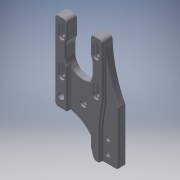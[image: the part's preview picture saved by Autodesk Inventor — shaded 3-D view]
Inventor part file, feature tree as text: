
AUTODESK INVENTOR PART (.ipt)
format: ipt  version: 2018 (Build 220112000, 112)  size: 500,224 bytes
history: native  units: in
note: dims shown in document units (in); Inventor stores cm internally (conversion verified against a paired STEP export)
features: extrude x12, sketch x12, projected_geometry x4, fillet x3, plane x2
ambient origin geometry x8: Origin, YZ Plane, XZ Plane, XY Plane, X Axis, Y Axis, Z Axis, Center Point
bodies: Solid1 (feature_tree)
feature tree (33):
  extrude  "Extrusion1"  Depth=1.6929in
  extrude  "Extrusion2"  Depth=0.4331in
  fillet  "Fillet1"  Radius=1.6535in
  extrude  "Extrusion3"  Depth=1.2205in
  extrude  "Extrusion4"  Depth=0.126in
  extrude  "Extrusion5"  Depth=0.315in
  extrude  "Extrusion6"  Depth=0.2362in TaperAngle=0.0deg
  plane  "Work Plane1"
  plane  "Work Plane2"
  extrude  "Extrusion7"  Depth=0.1575in TaperAngle=0.0deg
  extrude  "Extrusion8"  Depth=0.2362in
  extrude  "Extrusion9"  Depth=0.9449in
  extrude  "Extrusion10"  Depth=0.6102in
  extrude  "Extrusion11"  Depth=1.2992in
  extrude  "Extrusion12"  Depth=0.0394in
  fillet  "Fillet2"  Radius=7.0866in
  fillet  "Fillet4"  Radius=0.2362in
  sketch  "Sketch1"  dims[d0=3.8189in d1=1.6929in]
  sketch  "Sketch2"  dims[d2=0.4331in d3=0.4331in d4=1.6535in]
  sketch  "Sketch3"  dims[d5=0.1969in d6=0.0in d7=1.2205in]
  projected_geometry  "Projected Loop1"
  sketch  "Sketch4"  dims[d8=1.2205in d9=0.126in]
  projected_geometry  "Projected Loop2"
  sketch  "Sketch5"  dims[d10=0.2756in d11=0.315in]
  projected_geometry  "Projected Loop3"
  sketch  "Sketch6"  dims[d12=0.315in d13=0.2362in d14=0.0in]
  sketch  "Sketch8"  dims[d15=0.315in d16=0.1575in d17=0.0in]
  sketch  "Sketch9"  dims[d18=0.2362in d20=0.2362in]
  sketch  "Sketch10"  dims[d21=0.0787in d22=0.0in d23=0.9449in]
  projected_geometry  "Projected Loop4"
  sketch  "Sketch11"  dims[d24=0.315in d25=0.6102in]
  sketch  "Sketch12"  dims[d26=0.0in d27=0.0in d28=1.2992in]
  sketch  "Sketch13"  dims[d30=0.2362in d31=0.0in d32=0.1181in d33=7.0866in d34=0.2362in d35=0.0in d36=0.1654in d38=0.3937in d39=0.315in d40=0.4724in d41=0.2362in d42=0.0in d43=0.2165in d44=0.1654in d46=0.2165in d47=0.3937in d50=0.2362in d51=0.0in d52=0.2441in d53=0.0787in d54=0.0in d55=0.0787in d56=0.0in d57=0.7874in d58=0.3937in d59=0.7874in d60=0.0in d61=0.7874in d62=0.0in d63=0.1181in d65=0.0394in d69=1.063in]
